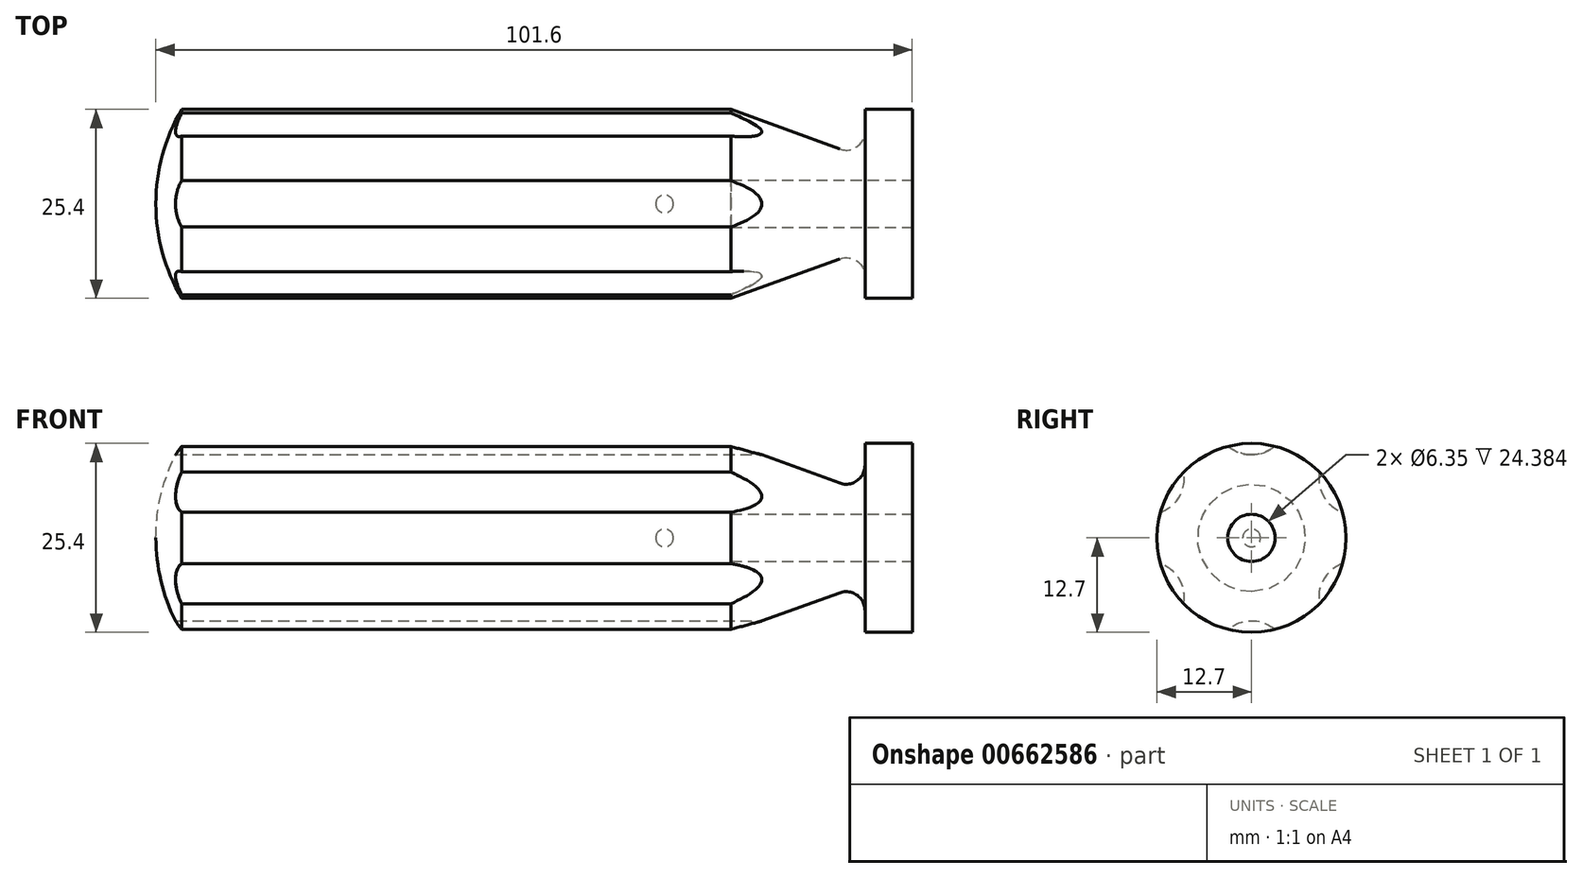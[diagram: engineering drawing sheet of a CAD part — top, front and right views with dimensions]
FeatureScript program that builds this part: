
annotation { "Feature Type Name" : "Feature", "Feature Type Description" : "" }
export const myFeature = defineFeature(function(context is Context, id is Id, definition is map)
    precondition{}
    {
        {
            var Q0;
            Q0=qCreatedBy(makeId("Front.planeOp"),FACE);
            var sketch = newSketch(context, id + "F0", { "sketchPlane" : qUnion([Q0])});
            skLineSegment(sketch, "E0.bottom", {"start": v(8.89, 0) * mm, "end": v(-68.33, 0) * mm});
            skLineSegment(sketch, "E0.top", {"start": v(33.27, 12.7) * mm, "end": v(26.92, 12.7) * mm});
            skLineSegment(sketch, "E0.left", {"start": v(33.27, 3.18) * mm, "end": v(33.27, 12.7) * mm});
            skArc(sketch, "E1", {"start": v(-64.87, 12.7) * mm, "mid": v(-67.45, 6.58) * mm, "end": v(-68.33, 0) * mm});
            skLineSegment(sketch, "E2", {"start": v(26.92, 12.7) * mm, "end": v(26.92, 9.76) * mm});
            skLineSegment(sketch, "E3", {"start": v(23.52, 7.38) * mm, "end": v(8.89, 12.7) * mm});
            skLineSegment(sketch, "E4.trimOffspring", {"start": v(8.89, 12.7) * mm, "end": v(-64.87, 12.7) * mm});
            skPoint(sketch, "E5.visualSharp", {"position": v(26.92, 6.14) * mm});
            skArc(sketch, "E5.filletArc", {"start": v(23.52, 7.38) * mm, "mid": v(25.84, 7.68) * mm, "end": v(26.92, 9.76) * mm});
            skLineSegment(sketch, "E6.top", {"start": v(33.27, 3.18) * mm, "end": v(8.89, 3.18) * mm});
            skLineSegment(sketch, "E6.right", {"start": v(8.89, 0) * mm, "end": v(8.89, 3.18) * mm});
            skCircle(sketch, "E7", {"center": v(0, 0) * mm, "radius": 1.2 * mm});
            skSolve(sketch);
        }
        {
            var Q0;
            Q0=qSketchRegion(id+"F0",true);
            var Q1;
            Q1=sQuery(id+"F0.wireOp",EDGE,"E0.bottom");
            revolve(context, id + "F1", {"entities" : qUnion([Q0]), "axis" : qUnion([Q1]), "revolveType" : RevolveType.FULL});
        }
        {
            var Q0;
            Q0=qSketchRegion(id+"F0",true);
            var Q1;
            Q1=sQuery(id+"F0.wireOp",EDGE,"E0.bottom");
            revolve(context, id + "F2", {"entities" : qUnion([Q0]), "axis" : qUnion([Q1]), "revolveType" : RevolveType.FULL});
        }
        {
            var Q0;
            Q0=makeQuery(id+"F1.opRevolve","SWEPT_FACE",FACE,{"disambiguationData":[OSD([sQuery(id+"F0.wireOp",EDGE,"E0.left")])]});
            var sketch = newSketch(context, id + "F3", { "sketchPlane" : qUnion([Q0])});
            skCircle(sketch, "E8", {"center": v(0, 0) * mm, "radius": 16 * mm, "construction": true});
            skCircle(sketch, "E9", {"center": v(0, 16) * mm, "radius": 4.83 * mm});
            skCircle(sketch, "E10.1.0", {"center": v(-13.86, 8) * mm, "radius": 4.83 * mm});
            skCircle(sketch, "E10.2.0", {"center": v(-13.86, -8) * mm, "radius": 4.83 * mm});
            skCircle(sketch, "E10.3.0", {"center": v(0, -16) * mm, "radius": 4.83 * mm});
            skCircle(sketch, "E10.4.0", {"center": v(13.86, -8) * mm, "radius": 4.83 * mm});
            skCircle(sketch, "E10.5.0", {"center": v(13.86, 8) * mm, "radius": 4.83 * mm});
            skSolve(sketch);
        }
        {
            var Q0;
            Q0=qSketchRegion(id+"F3",true);
            extrude(context, id + "F4", {"entities" : qUnion([Q0]), "operationType" : NewBodyOperationType.REMOVE, "oppositeDirection" : true, "depth" : 101.6 * mm, "offsetDistance" : 25.4 * mm, "hasSecondDirection" : true, "secondDirectionOppositeDirection" : true, "secondDirectionDepth" : 6.35 * mm});
        }
    });
